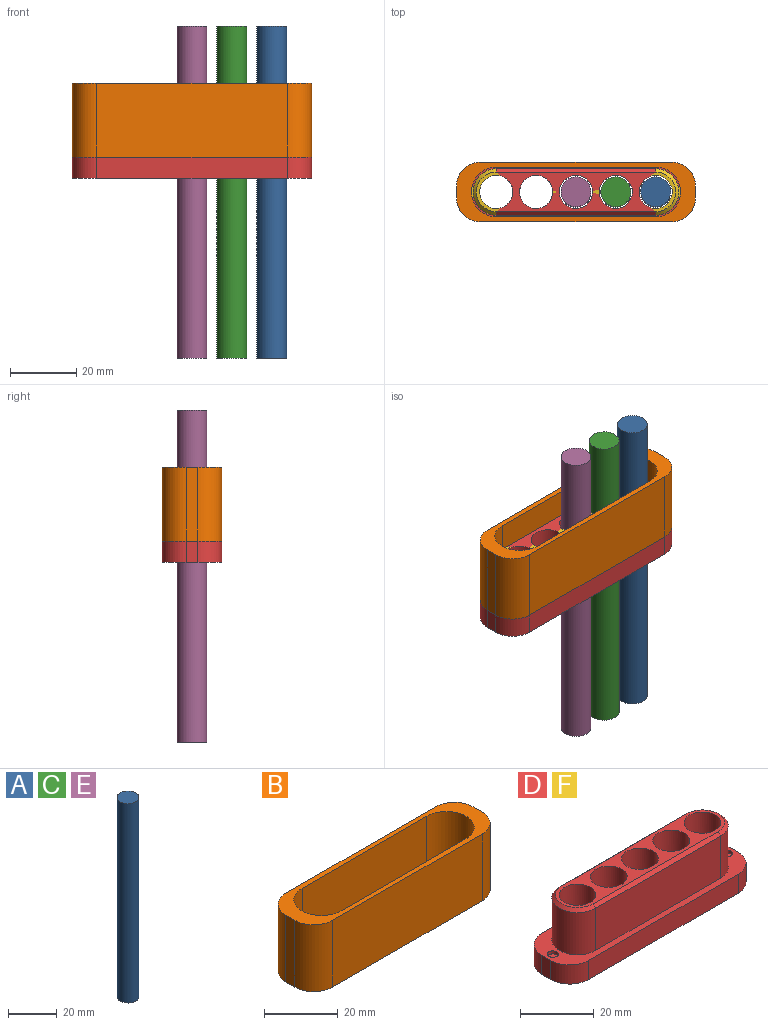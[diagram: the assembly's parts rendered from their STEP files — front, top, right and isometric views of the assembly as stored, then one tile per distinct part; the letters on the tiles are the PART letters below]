
ASSEMBLY  parts=6 mates=5
PART A: 3 faces, bbox 9x9x100 mm
  f0: cylinder r=4.5mm len=100mm, axis (0,0,-1), area 2827.4mm2, adj f1,f2
  f1: plane 9x9mm, normal (0,0,1), area 63.6mm2, adj f0
  f2: plane 9x9mm, normal (0,0,-1), area 63.6mm2, adj f0
PART B: 18 faces, bbox 72x18x22.3 mm
  f0: plane 22.25x3.5mm, normal (1,0,0), area 77.9mm2, adj f4,f5,f12,f17
  f1: plane 57.5x22.25mm, normal (0,-1,0), area 1279.4mm2, adj f5,f6,f12,f17
  f2: plane 57.5x22.25mm, normal (0,1,0), area 1279.4mm2, adj f4,f7,f12,f17
  f3: plane 22.25x3.5mm, normal (-1,0,0), area 77.9mm2, adj f6,f7,f12,f17
  f4: cylinder r=7.25mm len=22.25mm, axis (0,0,-1), area 253.4mm2, adj f0,f2,f12,f17
  f5: cylinder r=7.25mm len=22.25mm, axis (0,0,1), area 253.4mm2, adj f0,f1,f12,f17
  f6: cylinder r=7.25mm len=22.25mm, axis (0,0,-1), area 253.4mm2, adj f1,f3,f12,f17
  f7: cylinder r=7.25mm len=22.25mm, axis (0,0,1), area 253.4mm2, adj f2,f3,f12,f17
  f8: plane 48x22.25mm, normal (0,-1,0), area 1068mm2, adj f9,f11,f12,f17
  f9: cylinder r=7.5mm len=22.25mm, axis (0,0,-1), area 524.3mm2, adj f8,f10,f12,f17
  f10: plane 48x22.25mm, normal (0,1,0), area 1068mm2, adj f9,f11,f12,f17
  f11: cylinder r=7.5mm len=22.25mm, axis (0,0,-1), area 524.3mm2, adj f8,f10,f12,f17
  f12: plane 72x18mm, normal (0,0,-1), area 339.9mm2, adj f0,f1,f2,f3,f4,f5,f6,f7
  f13: cylinder r=1.51mm len=3.01mm, axis (0,0,-1), area 9.5mm2, adj f12,f14
  f14: plane 3.01x3.01mm, normal (0,0,-1), area 7.1mm2, adj f13
  f15: cylinder r=1.51mm len=3.01mm, axis (0,0,-1), area 9.5mm2, adj f12,f16
  f16: plane 3.01x3.01mm, normal (0,0,-1), area 7.1mm2, adj f15
  f17: plane 72x18mm, normal (0,0,1), area 354.2mm2, adj f0,f1,f2,f3,f4,f5,f6,f7
PART C: same geometry as A
PART D: 28 faces, bbox 72x18x21.4 mm
  f0: plane 72x18mm, normal (0,0,1), area 410.7mm2, adj f1,f2,f3,f4,f5,f6,f7,f8
  f1: plane 57.5x6.35mm, normal (0,1,0), area 365.1mm2, adj f0,f15,f18,f23
  f2: plane 6.35x3.5mm, normal (1,0,0), area 22.2mm2, adj f0,f15,f16,f23
  f3: plane 57.5x6.35mm, normal (0,-1,0), area 365.1mm2, adj f0,f16,f17,f23
  f4: plane 6.35x3.5mm, normal (-1,0,0), area 22.2mm2, adj f0,f17,f18,f23
  f5: plane 48x14mm, normal (0,1,0), area 672mm2, adj f0,f6,f8,f24
  f6: cylinder r=7mm len=14mm, axis (0,0,-1), area 307.9mm2, adj f0,f5,f7,f26
  f7: plane 48x14mm, normal (0,-1,0), area 672mm2, adj f0,f6,f8,f27
  f8: cylinder r=7mm len=14mm, axis (0,0,-1), area 307.9mm2, adj f0,f5,f7,f25
  f9: plane 60x12mm, normal (0,0,1), area 296.4mm2, adj f10,f11,f12,f13,f14,f24,f25,f26
  f10: cylinder r=5mm len=21.35mm, axis (0,0,-1), area 670.7mm2, adj f9,f23
  f11: cylinder r=5mm len=21.35mm, axis (0,0,-1), area 670.7mm2, adj f9,f23
  f12: cylinder r=5mm len=21.35mm, axis (0,0,-1), area 670.7mm2, adj f9,f23
  f13: cylinder r=5mm len=21.35mm, axis (0,0,-1), area 670.7mm2, adj f9,f23
  f14: cylinder r=5mm len=21.35mm, axis (0,0,-1), area 670.7mm2, adj f9,f23
  f15: cylinder r=7.25mm len=7.25mm, axis (0,0,1), area 72.3mm2, adj f0,f1,f2,f23
  f16: cylinder r=7.25mm len=7.25mm, axis (0,0,-1), area 72.3mm2, adj f0,f2,f3,f23
  f17: cylinder r=7.25mm len=7.25mm, axis (0,0,1), area 72.3mm2, adj f0,f3,f4,f23
  f18: cylinder r=7.25mm len=7.25mm, axis (0,0,-1), area 72.3mm2, adj f0,f1,f4,f23
  f19: cylinder r=1.51mm len=3.01mm, axis (0,0,1), area 9.5mm2, adj f0,f20
  f20: plane 3.01x3.01mm, normal (0,0,1), area 7.1mm2, adj f19
  f21: cylinder r=1.51mm len=3.01mm, axis (0,0,1), area 9.5mm2, adj f0,f22
  f22: plane 3.01x3.01mm, normal (0,0,1), area 7.1mm2, adj f21
  f23: plane 72x18mm, normal (0,0,-1), area 858.2mm2, adj f1,f2,f3,f4,f10,f11,f12,f13
  f24: plane 48x1mm, normal (0,0.71,0.71), area 67.9mm2, adj f5,f9,f25,f26
  f25: cone r=6mm half-angle=45deg, axis (0,0,-1), area 28.9mm2, adj f8,f9,f24,f27
  f26: cone r=6mm half-angle=45deg, axis (0,0,-1), area 28.9mm2, adj f6,f9,f24,f27
  f27: plane 48x1mm, normal (0,-0.71,0.71), area 67.9mm2, adj f7,f9,f25,f26
PART E: same geometry as A
PART F: same geometry as D
PLACE A rot(axis=(0,0,-1),90deg) t=(6.29,4.58,-17.35)mm
PLACE B t=(-17.71,4.58,-16.85)mm
PLACE C t=(-5.71,4.58,-17.35)mm
PLACE D t=(-17.71,4.58,-16.85)mm
PLACE E t=(-17.71,4.58,-17.35)mm
PLACE F t=(-17.71,4.58,-16.85)mm fixed
MATE fastened D.f8 <-> F.f8  axis (0,0,-1) through (6.29,4.58,36.8)mm
MATE slider E.f0 <-> F.f10  axis (0,0,-1) through (-17.71,4.58,-17.35)mm
MATE slider B.f13 <-> D.f21  axis (0,0,-1) through (15.79,4.58,43.15)mm
MATE slider C.f0 <-> F.f11  axis (0,0,-1) through (-5.71,4.58,-17.35)mm
MATE slider A.f0 <-> F.f8  axis (0,0,-1) through (6.29,4.58,-17.35)mm
